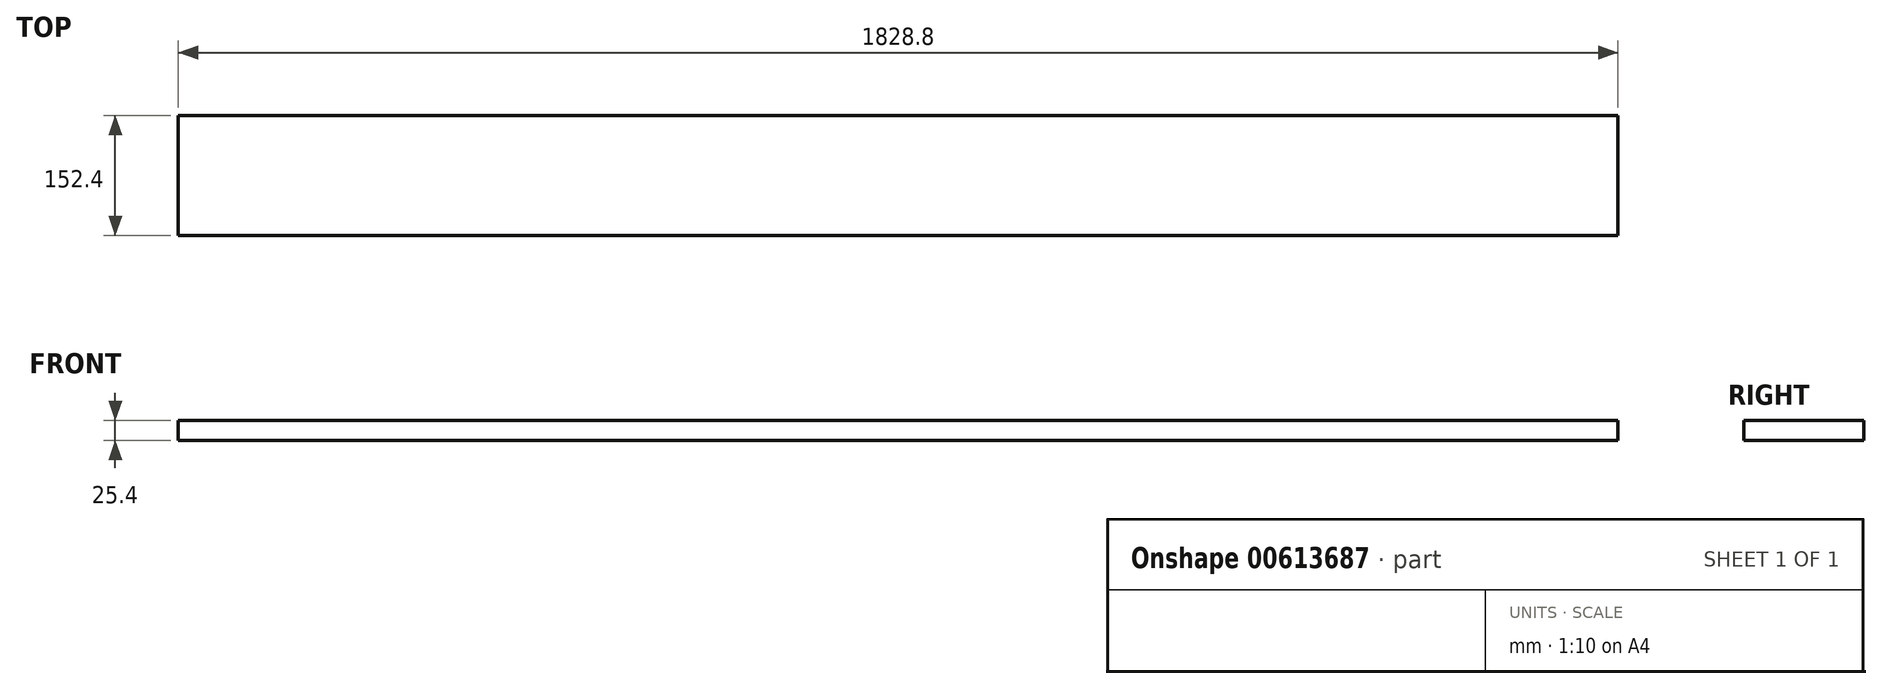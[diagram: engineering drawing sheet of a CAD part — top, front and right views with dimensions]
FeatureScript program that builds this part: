
annotation { "Feature Type Name" : "Feature", "Feature Type Description" : "" }
export const myFeature = defineFeature(function(context is Context, id is Id, definition is map)
    precondition{}
    {
        {
            var Q0;
            Q0=qCreatedBy(makeId("Top.planeOp"),FACE);
            var sketch = newSketch(context, id + "F0", { "sketchPlane" : qUnion([Q0])});
            skLineSegment(sketch, "E0.bottom", {"start": v(-894.59, -187.3) * mm, "end": v(934.21, -187.3) * mm});
            skLineSegment(sketch, "E0.top", {"start": v(-894.59, -339.7) * mm, "end": v(934.21, -339.7) * mm});
            skLineSegment(sketch, "E0.left", {"start": v(-894.59, -187.3) * mm, "end": v(-894.59, -339.7) * mm});
            skLineSegment(sketch, "E0.right", {"start": v(934.21, -187.3) * mm, "end": v(934.21, -339.7) * mm});
            skSolve(sketch);
        }
        {
            var Q0;
            Q0 = qSketchRegion(id + "F0", true);
            extrude(context, id + "F1", {"entities" : qUnion([Q0]), "depth" : 25.4 * mm, "offsetDistance" : 25.4 * mm});
        }
    });
